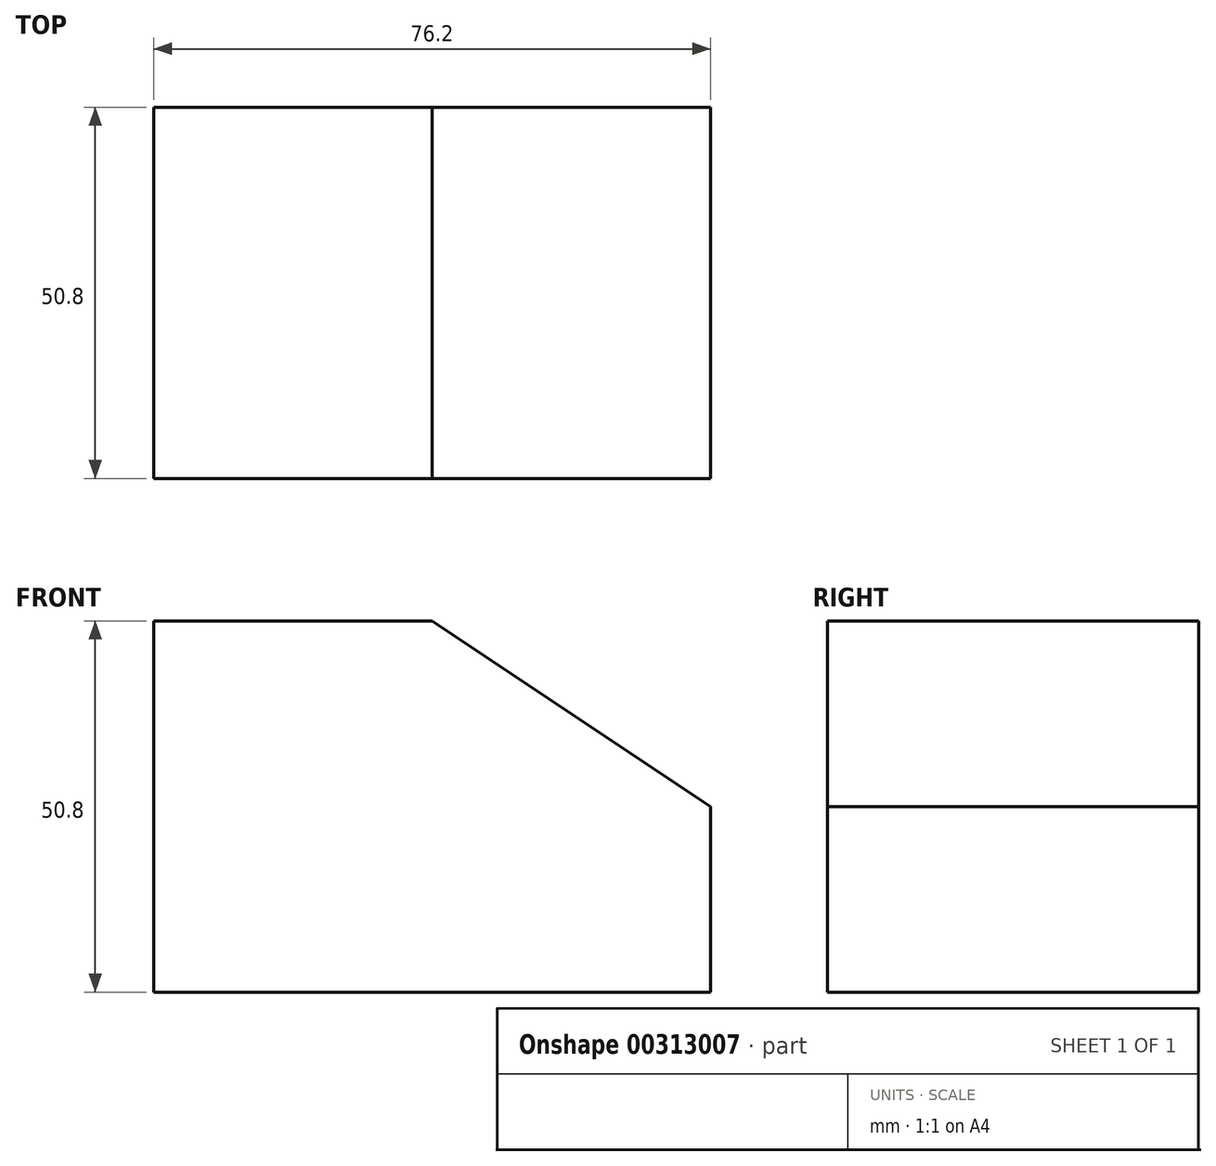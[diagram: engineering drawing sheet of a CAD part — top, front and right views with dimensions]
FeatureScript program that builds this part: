
annotation { "Feature Type Name" : "Feature", "Feature Type Description" : "" }
export const myFeature = defineFeature(function(context is Context, id is Id, definition is map)
    precondition{}
    {
        {
            var Q0;
            Q0=qCreatedBy(makeId("Front.planeOp"),FACE);
            var sketch = newSketch(context, id + "F0", { "sketchPlane" : qUnion([Q0])});
            skLineSegment(sketch, "E0", {"start": v(-30.49, -32.9) * mm, "end": v(45.71, -32.9) * mm});
            skLineSegment(sketch, "E1", {"start": v(45.71, -32.9) * mm, "end": v(45.71, -7.5) * mm});
            skLineSegment(sketch, "E2", {"start": v(45.71, -7.5) * mm, "end": v(7.61, 17.9) * mm});
            skLineSegment(sketch, "E3", {"start": v(7.61, 17.9) * mm, "end": v(-30.49, 17.9) * mm});
            skLineSegment(sketch, "E4", {"start": v(-30.49, 17.9) * mm, "end": v(-30.49, -32.9) * mm});
            skSolve(sketch);
        }
        {
            var Q0;
            Q0=makeQuery(id+"F0.imprint","IMPRINT",FACE,{"disambiguationData":[TD([[makeQuery(id+"F0.imprint","IMPRINT",EDGE,{"derivedFrom":sQuery(id+"F0.wireOp",EDGE,"E0")}),1.0]])]});
            extrude(context, id + "F1", {"entities" : qUnion([Q0]), "depth" : 50.8 * mm});
        }
    });
